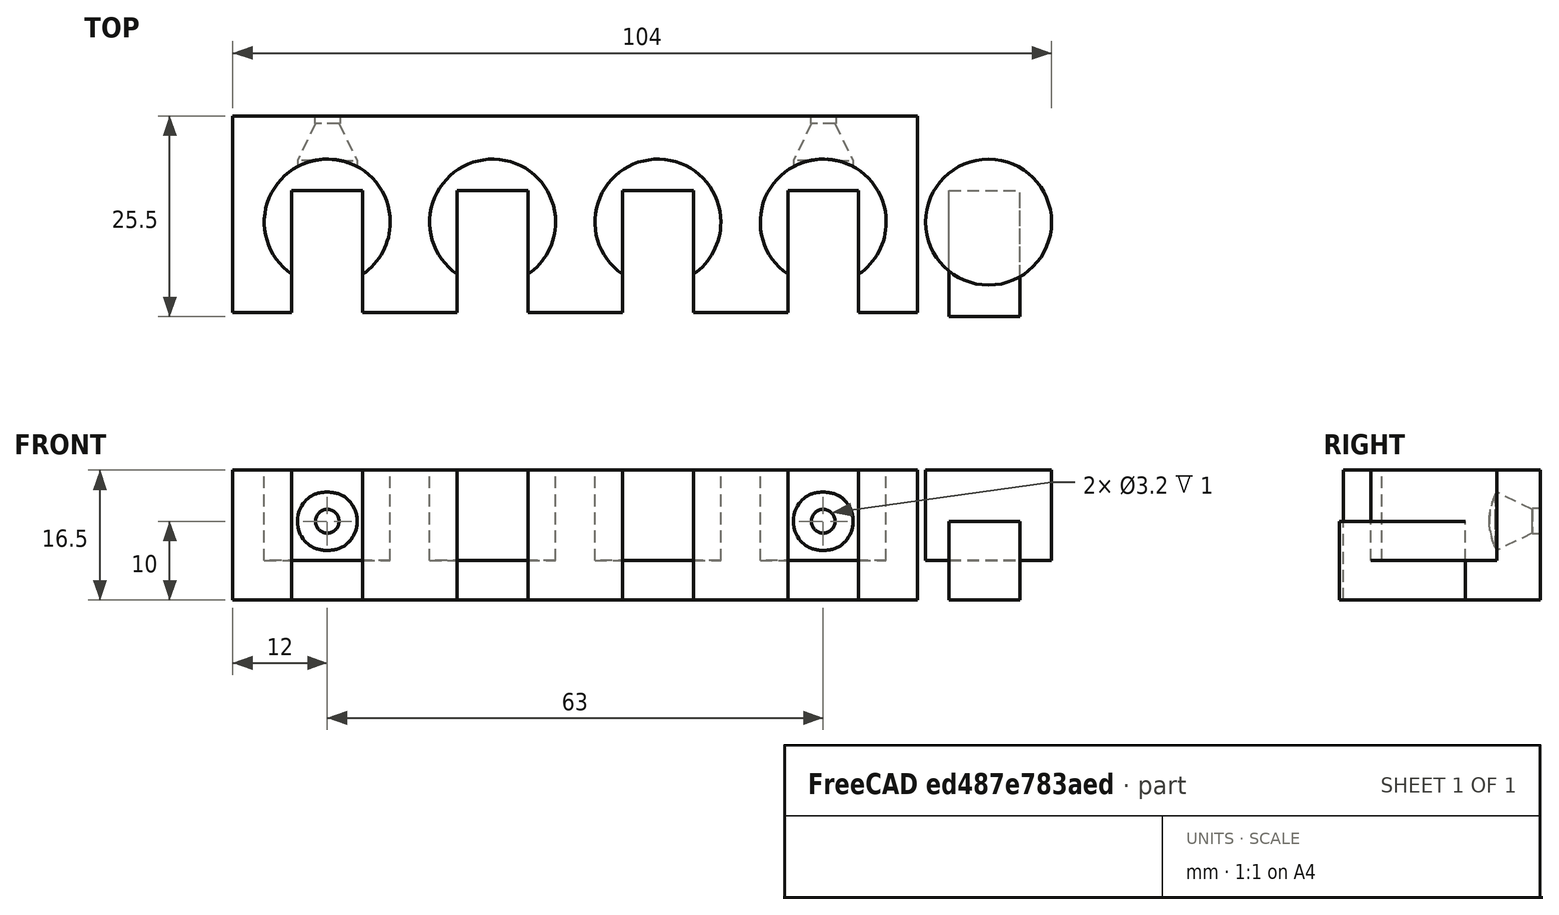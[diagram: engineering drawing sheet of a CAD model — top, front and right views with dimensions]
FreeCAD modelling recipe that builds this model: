
FCSTD DOCUMENT  (FreeCAD 0.14R3702 (Git))
Label: bnc_holder_xro
License: CC-BY 3.0
LicenseURL: http://creativecommons.org/licenses/by/3.0/
objects: Part::Cylinder×9, Part::Box×6, Part::MultiFuse×4, Part::Cut×2, Part::Cone×2
note: 23 computed .brp shape members not serialized (recipe doc carries the construction recipe); baked Part::Feature solids carry a one-line shape summary decoded from their .brp

FEATURE [Part::Box] Box  label="Cube"
  Height = 10
  Length = 9
  Placement = pos=(-5,-19,0) rot=(0,0,1;0rad)
  Width = 16
FEATURE [Part::Cylinder] Cylinder
  Angle = 360
  Height = 11.5
  Placement = pos=(0,-7,5) rot=(0,0,1;0rad)
  Radius = 8
FEATURE [Part::Box] Box001  label="MainBody"
  Height = 16.5
  Length = 87
  Placement = pos=(-96,-18.5,0) rot=(0,0,1;0rad)
  Width = 25
FEATURE [Part::Cylinder] Cylinder001
  Angle = 360
  Height = 11.5
  Placement = pos=(-21,-7,5) rot=(0,0,1;0rad)
  Radius = 8
FEATURE [Part::Box] Box002  label="Cube002"
  Height = 18
  Length = 9
  Placement = pos=(-25.5,-19,0) rot=(0,0,1;0rad)
  Width = 16
FEATURE [Part::Box] Box003  label="Cube003"
  Height = 18
  Length = 9
  Placement = pos=(-46.5,-19,0) rot=(0,0,1;0rad)
  Width = 16
FEATURE [Part::Cylinder] Cylinder002
  Angle = 360
  Height = 11.5
  Placement = pos=(-42,-7,5) rot=(0,0,1;0rad)
  Radius = 8
FEATURE [Part::Cylinder] Cylinder003
  Angle = 360
  Height = 11.5
  Placement = pos=(-63,-7,5) rot=(0,0,1;0rad)
  Radius = 8
FEATURE [Part::Box] Box004  label="Cube004"
  Height = 18
  Length = 9
  Placement = pos=(-67.5,-19,0) rot=(0,0,1;0rad)
  Width = 16
FEATURE [Part::Cylinder] Cylinder004
  Angle = 360
  Height = 11.5
  Placement = pos=(-84,-7,5) rot=(0,0,1;0rad)
  Radius = 8
FEATURE [Part::Box] Box005  label="Cube005"
  Height = 18
  Length = 9
  Placement = pos=(-88.5,-19,0) rot=(0,0,1;0rad)
  Width = 16
FEATURE [Part::MultiFuse] Fusion
  Shapes = -> [Cylinder001,Box002,Cylinder002,Box005,Cylinder003,Cylinder004,Box003,Box004]
FEATURE [Part::Cut] Cut
  Base = -> Box001
  Tool = -> Fusion
FEATURE [Part::Cylinder] Cylinder005
  Angle = 360
  Height = 10
  Placement = pos=(-21,10,10) rot=(1,0,0;1.5708rad)
  Radius = 1.6
FEATURE [Part::Cone] Cone
  Angle = 360
  Height = 4.7
  Placement = pos=(-21,0,10) rot=(1,0,0;1.5708rad)
  Radius1 = 1.5
  Radius2 = 3.8
FEATURE [Part::Cylinder] Cylinder006
  Angle = 360
  Height = 2
  Placement = pos=(-21,-4.7,10) rot=(1,0,0;1.5708rad)
  Radius = 3.8
FEATURE [Part::MultiFuse] Fusion004  label="Schraubenloch"
  Placement = pos=(0,5.5,0) rot=(0,0,1;0rad)
  Shapes = -> [Cylinder006,Cone,Cylinder005]
FEATURE [Part::Cone] Cone001
  Angle = 360
  Height = 4.7
  Placement = pos=(-21,0,10) rot=(1,0,0;1.5708rad)
  Radius1 = 1.5
  Radius2 = 3.8
FEATURE [Part::Cylinder] Cylinder007
  Angle = 360
  Height = 10
  Placement = pos=(-21,10,10) rot=(1,0,0;1.5708rad)
  Radius = 1.6
FEATURE [Part::Cylinder] Cylinder008
  Angle = 360
  Height = 2
  Placement = pos=(-21,-4.7,10) rot=(1,0,0;1.5708rad)
  Radius = 3.8
FEATURE [Part::MultiFuse] Fusion005  label="Schraubenloch001"
  Placement = pos=(-63,5.5,0) rot=(0,0,1;0rad)
  Shapes = -> [Cylinder008,Cone001,Cylinder007]
FEATURE [Part::MultiFuse] Fusion006  label="Schraubenloecher"
  Shapes = -> [Fusion005,Fusion004]
FEATURE [Part::Cut] Cut001
  Base = -> Cut
  Tool = -> Fusion006
